# Revit family: Decibel
name_source: partatom
category: Мебель
revit_build: Autodesk Revit 2017 (Build: 20160225_1515(x64)
units: mm (PartAtom-declared; Revit-internal decimal feet)

## family parameters
Всегда вертикально = Да
Заголовок OmniClass = General Furniture and Specialties
На основе рабочей плоскости = Нет
Номер OmniClass = 23.40.20.00
Общий = Нет
При загрузке вырезать с полостями = Нет
Точка расчета площади = Нет

## types (9) — shared parameters
URL = http://www.skandiform.com
Изготовитель = Skandiform AB
Ключевая пометка = XBF.2
Комментарии к типоразмеру = Created by Astacus AB

## per-type parameters (varying)
| type | Type | URL 2 |
| KS-105 | Decibel : KS-105 | http://file-system.ru |
| KS-107 | Decibel : KS-107 |  |
| S-005 | Decibel : S-005 |  |
| S-006 | Decibel : S-006 |  |
| S-007 | Decibel : S-007 |  |
| S-025 | Decibel : S-025 |  |
| KS-106 | Decibel : KS-106 |  |
| S-026 | Decibel : S-026 |  |
| S-027 | Decibel : S-027 |  |

note: column(s) folded — value = type name in every type: Группа модели

## geometry (parser evidence)
native form markers: Sweep x5
no freeform markers — native parametric forms only
